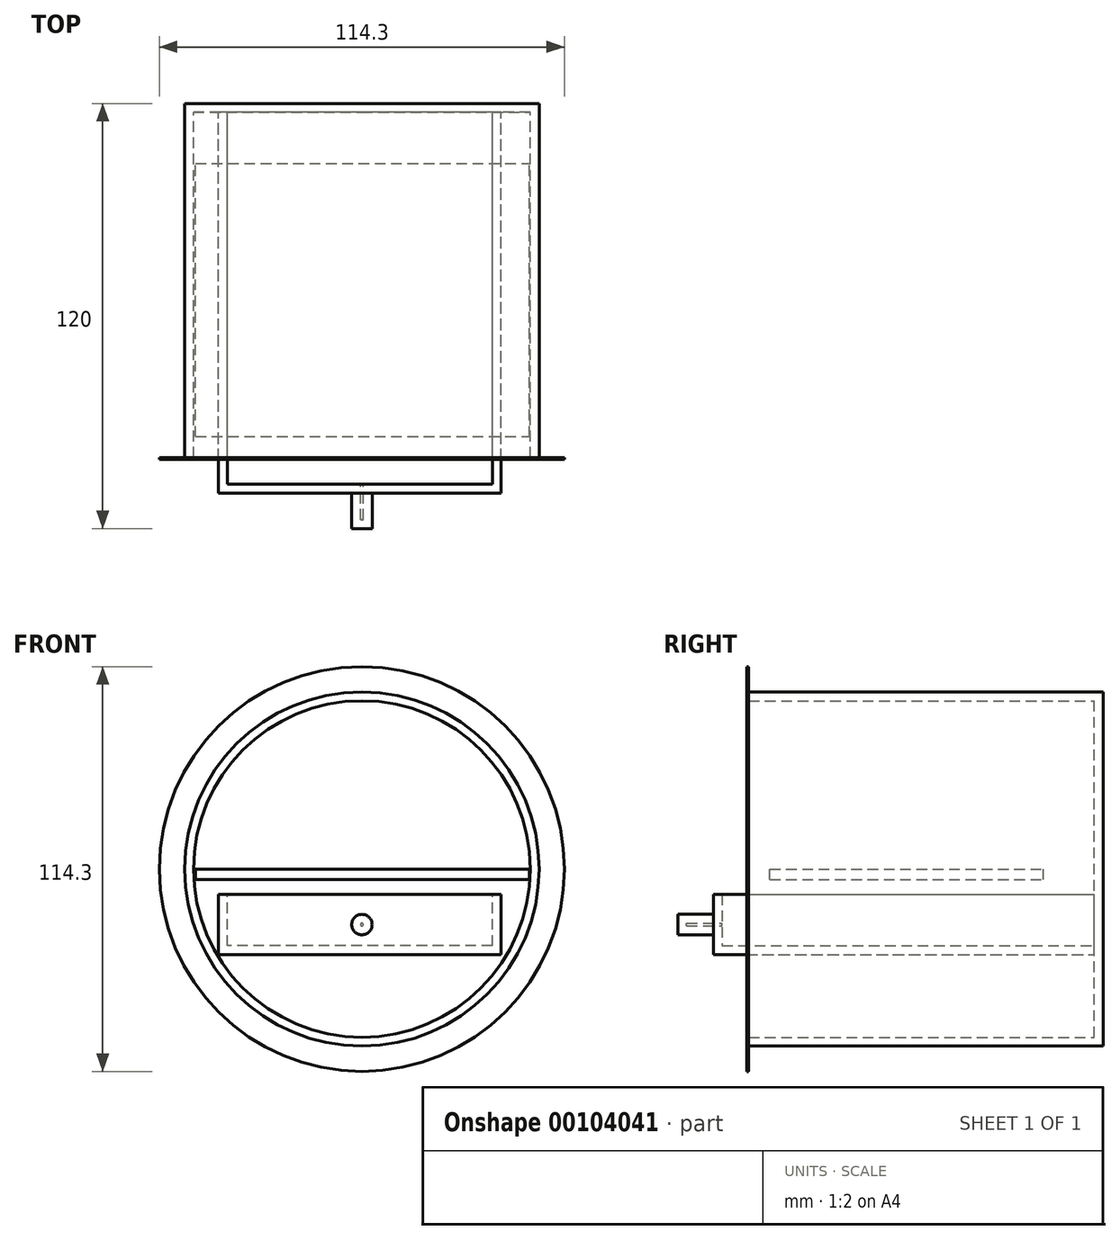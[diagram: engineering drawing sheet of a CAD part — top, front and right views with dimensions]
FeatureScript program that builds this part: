
annotation { "Feature Type Name" : "Feature", "Feature Type Description" : "" }
export const myFeature = defineFeature(function(context is Context, id is Id, definition is map)
    precondition{}
    {
        {
            var Q0;
            Q0=qCreatedBy(makeId("Front.planeOp"),FACE);
            var sketch = newSketch(context, id + "F0", { "sketchPlane" : qUnion([Q0])});
            skCircle(sketch, "E0", {"center": v(0, 0) * mm, "radius": 50 * mm});
            skSolve(sketch);
        }
        {
            var Q0;
            Q0 = qSketchRegion(id + "F97SOjj7pX8YPbt_0", true);
            var Q1;
            Q1 = qSketchRegion(id + "F0", true);
            extrude(context, id + "F1", {"entities" : qUnion([Q0, Q1]), "depth" : 100 * mm});
        }
        {
            var Q0;
            Q0=makeQuery(id+"F1.opExtrude","CAP_FACE",FACE,{"disambiguationData":[OSD([sQuery(id+"F0.wireOp",EDGE,"E0")])],"isStart":false});
            shell(context, id + "F2", {"entities" : qUnion([Q0]), "thickness" : 2.5 * mm});
        }
        {
            var Q0;
            Q0=qCreatedBy(makeId("Top.planeOp"),FACE);
            var sketch = newSketch(context, id + "F3", { "sketchPlane" : qUnion([Q0])});
            skLineSegment(sketch, "E1.bottom", {"start": v(-46.95, -94.06) * mm, "end": v(47.23, -94.06) * mm});
            skLineSegment(sketch, "E1.top", {"start": v(-46.95, -16.91) * mm, "end": v(47.23, -16.91) * mm});
            skLineSegment(sketch, "E1.left", {"start": v(-46.95, -94.06) * mm, "end": v(-46.95, -16.91) * mm});
            skLineSegment(sketch, "E1.right", {"start": v(47.23, -94.06) * mm, "end": v(47.23, -16.91) * mm});
            skSolve(sketch);
        }
        {
            var Q0;
            Q0=makeQuery(id+"F3.imprint","IMPRINT",FACE,{"disambiguationData":[TD([[makeQuery(id+"F3.imprint","IMPRINT",EDGE,{"derivedFrom":sQuery(id+"F3.wireOp",EDGE,"E1.bottom")}),1.0]])]});
            extrude(context, id + "F4", {"entities" : qUnion([Q0]), "operationType" : NewBodyOperationType.ADD, "oppositeDirection" : true, "depth" : 3 * mm});
        }
        {
            var Q0;
            Q0=qCreatedBy(makeId("Front.planeOp"),FACE);
            var sketch = newSketch(context, id + "F5", { "sketchPlane" : qUnion([Q0])});
            skLineSegment(sketch, "E2", {"start": v(-46.93, -6.6) * mm, "end": v(45.75, -6.6) * mm});
            skLineSegment(sketch, "E3", {"start": v(45.75, -6.6) * mm, "end": v(39.3, -24.78) * mm});
            skLineSegment(sketch, "E4", {"start": v(39.3, -24.78) * mm, "end": v(-38.42, -24.78) * mm});
            skLineSegment(sketch, "E5", {"start": v(-38.42, -24.78) * mm, "end": v(-46.93, -6.6) * mm});
            skSolve(sketch);
        }
        {
            var Q0;
            Q0=sQuery(id+"F5.wireOp",EDGE,"E2");
            var Q1;
            Q1=sQuery(id+"F5.wireOp",EDGE,"E5");
            var Q2;
            Q2=sQuery(id+"F5.wireOp",EDGE,"E4");
            var Q3;
            Q3=sQuery(id+"F5.wireOp",EDGE,"E3");
            extrude(context, id + "F6", {"bodyType" : ToolBodyType.SURFACE, "surfaceEntities" : qUnion([Q0, Q1, Q2, Q3]), "depth" : 100 * mm});
        }
        {
            var Q0;
            Q0=qCreatedBy(makeId("Front.planeOp"),FACE);
            var sketch = newSketch(context, id + "F7", { "sketchPlane" : qUnion([Q0])});
            skLineSegment(sketch, "E6.bottom", {"start": v(-40.47, -7.19) * mm, "end": v(39.3, -7.19) * mm});
            skLineSegment(sketch, "E6.top", {"start": v(-40.47, -24.2) * mm, "end": v(39.3, -24.2) * mm});
            skLineSegment(sketch, "E6.left", {"start": v(-40.47, -7.19) * mm, "end": v(-40.47, -24.2) * mm});
            skLineSegment(sketch, "E6.right", {"start": v(39.3, -7.19) * mm, "end": v(39.3, -24.2) * mm});
            skSolve(sketch);
        }
        {
            var Q0;
            Q0 = qSketchRegion(id + "F7", true);
            var Q1;
            Q1=sQuery(id+"F7.wireOp",EDGE,"E6.left");
            var Q2;
            Q2=sQuery(id+"F7.wireOp",EDGE,"E6.bottom");
            var Q3;
            Q3=sQuery(id+"F7.wireOp",EDGE,"E6.right");
            var Q4;
            Q4=sQuery(id+"F7.wireOp",EDGE,"E6.top");
            extrude(context, id + "F8", {"entities" : qUnion([Q0]), "operationType" : NewBodyOperationType.ADD, "surfaceEntities" : qUnion([Q1, Q2, Q3, Q4]), "depth" : 110 * mm});
        }
        {
            var Q0;
            Q0=makeQuery(id+"F8.opExtrude","CAP_FACE",FACE,{"disambiguationData":[OSD([sQuery(id+"F7.wireOp",EDGE,"E6.bottom"),sQuery(id+"F7.wireOp",EDGE,"E6.top"),sQuery(id+"F7.wireOp",EDGE,"E6.left"),sQuery(id+"F7.wireOp",EDGE,"E6.right")])],"isStart":false});
            var sketch = newSketch(context, id + "F9", { "sketchPlane" : qUnion([Q0])});
            skCircle(sketch, "E7", {"center": v(0, -15.7) * mm, "radius": 2.89 * mm});
            skSolve(sketch);
        }
        {
            var Q0;
            Q0=makeQuery(id+"F9.imprint","IMPRINT",FACE,{"disambiguationData":[TD([[makeQuery(id+"F9.imprint","IMPRINT",EDGE,{"derivedFrom":sQuery(id+"F9.wireOp",EDGE,"E7")}),1.0]])]});
            extrude(context, id + "F10", {"entities" : qUnion([Q0]), "operationType" : NewBodyOperationType.ADD, "depth" : 10 * mm});
        }
        {
            var Q0;
            Q0=qCreatedBy(makeId("Front.planeOp"),FACE);
            var sketch = newSketch(context, id + "F11", { "sketchPlane" : qUnion([Q0])});
            skCircle(sketch, "E8", {"center": v(0, 0) * mm, "radius": 50.53 * mm});
            skSolve(sketch);
        }
        {
            var Q0;
            Q0=makeQuery(id+"F8.opExtrude","SWEPT_FACE",FACE,{"disambiguationData":[OSD([sQuery(id+"F7.wireOp",EDGE,"E6.bottom")])]});
            shell(context, id + "F12", {"entities" : qUnion([Q0]), "thickness" : 2.5 * mm});
        }
        {
            var Q0;
            Q0=makeQuery(id+"F1.opExtrude","CAP_FACE",FACE,{"disambiguationData":[OSD([sQuery(id+"F0.wireOp",EDGE,"E0")])],"isStart":false});
            var sketch = newSketch(context, id + "F13", { "sketchPlane" : qUnion([Q0])});
            skCircle(sketch, "E9", {"center": v(0, 0) * mm, "radius": 57.15 * mm});
            skSolve(sketch);
        }
        {
            var Q0;
            Q0=makeQuery(id+"F13.imprint","IMPRINT",FACE,{"disambiguationData":[TD([[makeQuery(id+"F13.imprint","IMPRINT",EDGE,{"derivedFrom":sQuery(id+"F13.wireOp",EDGE,"E9")}),1.0]])]});
            var Q1;
            Q1=sQuery(id+"F13.wireOp",EDGE,"E9");
            extrude(context, id + "F14", {"entities" : qUnion([Q0]), "surfaceEntities" : qUnion([Q1]), "depth" : 0.5 * mm});
        }
    });
